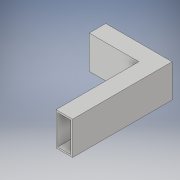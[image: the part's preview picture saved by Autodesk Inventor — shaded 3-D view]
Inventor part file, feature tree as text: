
AUTODESK INVENTOR PART (.ipt)
format: ipt  version: 2018 (Build 220112000, 112)  size: 129,536 bytes
history: native  units: in
note: dims shown in document units (in); Inventor stores cm internally (conversion verified against a paired STEP export)
features: extrude x3, sketch x3
ambient origin geometry x8: Origin, YZ Plane, XZ Plane, XY Plane, X Axis, Y Axis, Z Axis, Center Point
bodies: Body1 (feature_tree)
feature tree (6):
  extrude  "Extrusion12"  Depth=2.0in
  extrude  "Extrusion13"  Depth=0.1in
  extrude  "Extrusion14"  Depth=0.1in
  sketch  "Sketch15"  dims[d46=1.0in d47=2.0in]
  sketch  "Sketch16"  dims[d48=0.1in d49=0.1in]
  sketch  "Sketch17"  dims[d50=0.1in d51=0.1in d52=3.0in d53=0.0in d54=1.0in d55=2.0in d56=0.1in d57=0.1in d58=0.1in d59=0.1in d60=6.0in d61=0.0in d62=0.1in d63=0.0in]
